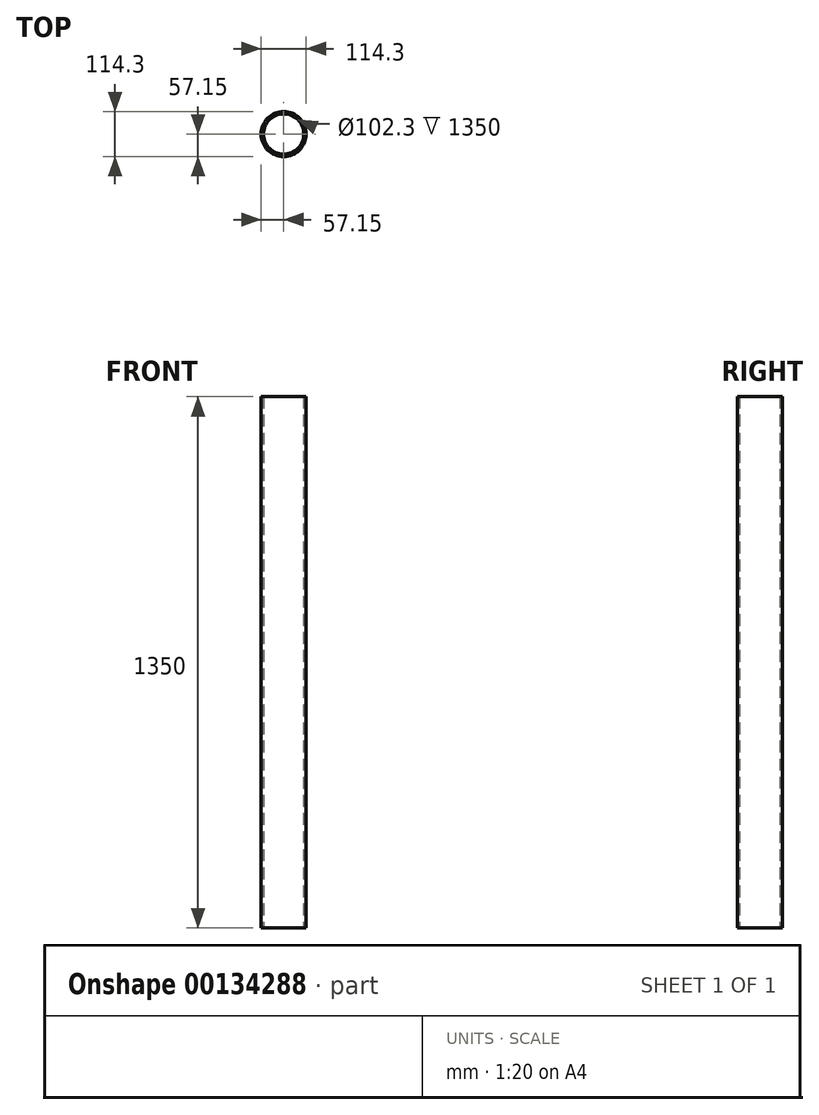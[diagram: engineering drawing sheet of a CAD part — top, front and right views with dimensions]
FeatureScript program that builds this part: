
annotation { "Feature Type Name" : "Feature", "Feature Type Description" : "" }
export const myFeature = defineFeature(function(context is Context, id is Id, definition is map)
    precondition{}
    {
        {
            var Q0;
            Q0=qCreatedBy(makeId("Top.planeOp"),FACE);
            var sketch = newSketch(context, id + "F0", { "sketchPlane" : qUnion([Q0])});
            skCircle(sketch, "E0", {"center": v(0, 0) * mm, "radius": 57.15 * mm});
            skSolve(sketch);
        }
        {
            var Q0;
            Q0 = qSketchRegion(id + "F0", true);
            extrude(context, id + "F1", {"entities" : qUnion([Q0]), "depth" : 1350 * mm});
        }
        {
            var Q0;
            Q0=makeQuery(id+"F1.opExtrude","CAP_FACE",FACE,{"disambiguationData":[OSD([sQuery(id+"F0.wireOp",EDGE,"E0")])],"isStart":true});
            var Q1;
            Q1=makeQuery(id+"F1.opExtrude","CAP_FACE",FACE,{"disambiguationData":[OSD([sQuery(id+"F0.wireOp",EDGE,"E0")])],"isStart":false});
            shell(context, id + "F2", {"entities" : qUnion([Q0, Q1]), "thickness" : 6 * mm});
        }
    });
